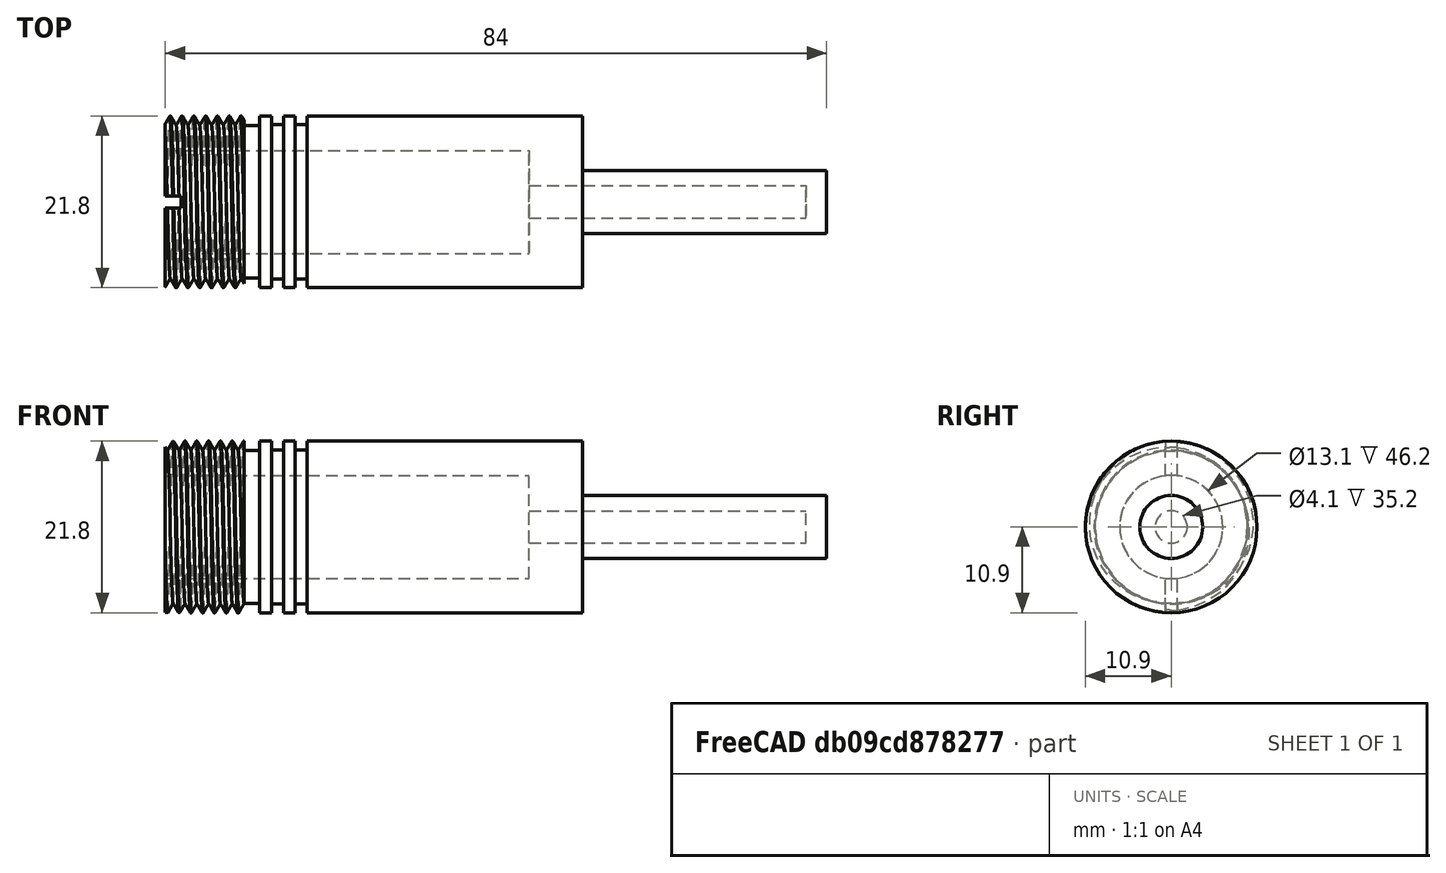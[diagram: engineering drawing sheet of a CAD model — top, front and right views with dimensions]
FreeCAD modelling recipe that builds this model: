
FCSTD DOCUMENT  (FreeCAD 0.17R13541 (Git))
Label: ERG-T-03-SH-01
License: All rights reserved
LicenseURL: http://en.wikipedia.org/wiki/All_rights_reserved
objects: Drawing::FeatureViewPython×25, Part::Cylinder×16, Part::Cut×11, Part::MultiFuse×4, Part::Helix×1, Sketcher::SketchObject×1, Part::Sweep×1, Part::Box×1, Drawing::FeatureViewPart×1, Drawing::FeaturePage×1
note: 35 computed .brp shape members not serialized (recipe doc carries the construction recipe); baked Part::Feature solids carry a one-line shape summary decoded from their .brp

FEATURE [Part::Cylinder] Cylinder072  label="Cylinder077"
  Angle = 360
  AttacherType = Attacher::AttachEngine3D
  Height = 18
  Placement = pos=(180.5,0,0) rot=(0,1,0;1.5708rad)
  Radius = 10.9
FEATURE [Part::Cylinder] Cylinder074  label="Cylinder083"
  Angle = 360
  AttacherType = Attacher::AttachEngine3D
  Height = 46.2
  Placement = pos=(180.5,0,0) rot=(0,1,0;1.5708rad)
  Radius = 6.55
FEATURE [Part::Cylinder] Cylinder075  label="Cylinder084"
  Angle = 360
  AttacherType = Attacher::AttachEngine3D
  Height = 53
  Placement = pos=(180.5,0,0) rot=(0,1,0;1.5708rad)
  Radius = 12.5
FEATURE [Part::Cylinder] Cylinder076  label="Cylinder085"
  Angle = 360
  AttacherType = Attacher::AttachEngine3D
  Height = 18
  Placement = pos=(180.5,0,0) rot=(0,1,0;1.5708rad)
  Radius = 12.5
FEATURE [Part::Cylinder] Cylinder077  label="Cylinder086"
  Angle = 360
  AttacherType = Attacher::AttachEngine3D
  Height = 31
  Placement = pos=(233.5,0,0) rot=(0,1,0;1.5708rad)
  Radius = 4
FEATURE [Part::Cut] Cut065
  Base = -> Cylinder076
  Tool = -> Cylinder072
FEATURE [Part::Cylinder] Cylinder080  label="Cylinder089"
  Angle = 360
  AttacherType = Attacher::AttachEngine3D
  Height = 35.2
  Placement = pos=(226.7,0,0) rot=(0,1,0;1.5708rad)
  Radius = 2.05
FEATURE [Part::MultiFuse] Fusion017  label="cavity"
  Shapes = -> [Cylinder080,Cylinder074]
FEATURE [Part::Helix] Helix019
  Angle = 0
  AttacherType = Attacher::AttachEngine3D
  Height = 17
  LocalCoord = 0
  Pitch = 1.5
  Placement = pos=(157,0,0) rot=(0,1,0;1.5708rad)
  Radius = 10.5
  Style = 1
FEATURE [Sketcher::SketchObject] Sketch023  label="T022"
  Placement = pos=(157,0,-11.01) rot=(1,0,0;1.5708rad)
  sketch-geometry (3):
    g0: LineSegment StartX=0 StartY=1.29904 StartZ=0 EndX=-0.75 EndY=0 EndZ=0
    g1: LineSegment StartX=0.75 StartY=0 StartZ=0 EndX=0 EndY=1.29904 EndZ=0
    g2: LineSegment StartX=-0.75 StartY=0 StartZ=0 EndX=0.75 EndY=0 EndZ=0
  constraints (9):
    c: PointOnObject(g1,g-1)
    c: Coincident(g1,g0)
    c: Coincident(g2,g0)
    c: Coincident(g2,g1)
    c: Horizontal(g2)
    c: Symmetric(g0,g1,g-2)
    c: Distance(g0,g1) = 1.5
    c: Angle(g1,g2) = 1.0472
    c: Angle(g2,g0) = 1.0472
FEATURE [Part::Sweep] Sweep016
  Frenet = true
  Sections = -> [Sketch023]
  Solid = true
  Spine = -> Helix019
  Transition = 1
FEATURE [Part::Cylinder] Cylinder084  label="Cylinder092"
  Angle = 360
  AttacherType = Attacher::AttachEngine3D
  Height = 1.5
  Placement = pos=(178,0,0) rot=(0,1,0;1.5708rad)
  Radius = 11
FEATURE [Part::Cylinder] Cylinder085  label="Cylinder093"
  Angle = 360
  AttacherType = Attacher::AttachEngine3D
  Height = 1.5
  Placement = pos=(178,0,0) rot=(0,1,0;1.5708rad)
  Radius = 9.8
FEATURE [Part::Cut] Cut071  label="circ2"
  Base = -> Cylinder084
  Placement = pos=(16,0,0) rot=(0,0,1;0rad)
  Tool = -> Cylinder085
FEATURE [Part::Cylinder] Cylinder086  label="Cylinder094"
  Angle = 360
  AttacherType = Attacher::AttachEngine3D
  Height = 2
  Placement = pos=(178,0,0) rot=(0,1,0;1.5708rad)
  Radius = 11
FEATURE [Part::Cylinder] Cylinder087  label="Cylinder095"
  Angle = 360
  AttacherType = Attacher::AttachEngine3D
  Height = 2
  Placement = pos=(178,0,0) rot=(0,1,0;1.5708rad)
  Radius = 9.7
FEATURE [Part::Cut] Cut072  label="circ1"
  Base = -> Cylinder086
  Placement = pos=(12.5,0,0) rot=(0,0,1;0rad)
  Tool = -> Cylinder087
FEATURE [Part::Cylinder] Cylinder088  label="Cylinder096"
  Angle = 360
  AttacherType = Attacher::AttachEngine3D
  Height = 10
  Placement = pos=(178,0,0) rot=(0,1,0;1.5708rad)
  Radius = 9
FEATURE [Part::Cylinder] Cylinder089  label="Cylinder097"
  Angle = 360
  AttacherType = Attacher::AttachEngine3D
  Height = 10
  Placement = pos=(178,0,0) rot=(0,1,0;1.5708rad)
  Radius = 11.5
FEATURE [Part::Cut] Cut074
  Base = -> Cylinder089
  Placement = pos=(-10.5,0,0) rot=(0,0,1;0rad)
  Tool = -> Cylinder088
FEATURE [Part::Box] Box  label="Cube"
  AttacherType = Attacher::AttachEngine3D
  Height = 30
  Length = 2
  Placement = pos=(180.5,-0.75,-15) rot=(0,0,1;0rad)
  Width = 1.5
FEATURE [Part::Cylinder] Cylinder091  label="Cylinder099"
  Angle = 360
  AttacherType = Attacher::AttachEngine3D
  Height = 35
  Placement = pos=(198.5,0,0) rot=(0,1,0;1.5708rad)
  Radius = 12.5
FEATURE [Part::Cylinder] Cylinder092  label="Cylinder100"
  Angle = 360
  AttacherType = Attacher::AttachEngine3D
  Height = 35
  Placement = pos=(198.5,0,0) rot=(0,1,0;1.5708rad)
  Radius = 10.9
FEATURE [Part::Cut] Cut
  Base = -> Cylinder091
  Tool = -> Cylinder092
FEATURE [Part::Cylinder] Cylinder093  label="Cylinder101"
  Angle = 360
  AttacherType = Attacher::AttachEngine3D
  Height = 1.5
  Placement = pos=(178,0,0) rot=(0,1,0;1.5708rad)
  Radius = 11
FEATURE [Part::Cylinder] Cylinder094  label="Cylinder102"
  Angle = 360
  AttacherType = Attacher::AttachEngine3D
  Height = 1.5
  Placement = pos=(178,0,0) rot=(0,1,0;1.5708rad)
  Radius = 9.8
FEATURE [Part::Cut] Cut076  label="circ3"
  Base = -> Cylinder093
  Placement = pos=(19,0,0) rot=(0,0,1;0rad)
  Tool = -> Cylinder094
FEATURE [Part::MultiFuse] Fusion019
  Shapes = -> [Cut,Cut065]
FEATURE [Part::MultiFuse] Fusion020
  Shapes = -> [Cylinder075,Cylinder077]
FEATURE [Part::Cut] Cut077  label="body"
  Base = -> Fusion020
  Tool = -> Fusion019
FEATURE [Part::Cut] Cut078  label="thread"
  Base = -> Sweep016
  Placement = pos=(23,0,0) rot=(0,0,1;0rad)
  Tool = -> Cut074
FEATURE [Part::MultiFuse] Fusion021  label="cutstuff"
  Shapes = -> [Cut078,Cut076,Cut072,Cut071]
FEATURE [Part::Cut] Cut079  label="outside"
  Base = -> Cut077
  Tool = -> Fusion021
FEATURE [Part::Cut] Cut080  label="holder01"
  Base = -> Cut079
  Tool = -> Fusion017
FEATURE [Part::Cut] Cut081  label="HOLDER"
  Base = -> Cut080
  Tool = -> Box
FEATURE [Drawing::FeatureViewPart] Ortho  label="Ortho_0_0"
  Direction = (0,1,0)
  HiddenWidth = 0.15
  LineWidth = 0.35
  Rotation = 90
  Scale = 2
  ShowHiddenLines = true
  ShowSmoothLines = false
  Source = -> Cut081
  Tolerance = 0.05
  ViewResult = <blob: 32842 chars omitted>
  Visible = false
  X = -316.2
  Y = 76.2849
FEATURE [Drawing::FeatureViewPython] dim001  # drawing view (typed FeaturePython)
  Rotation = 0
  ViewResult = <g> \n  <line x1="150.200000" y1="54.284900" x2="251.877041" y2="54.284900" style="stroke:rgb(255,0,0);stroke-width:0.10" />\n<line x1="150.200000" y1="98.284900" x2="251.877041" y2="98.284900" style="stroke:rgb(255,0,0);stroke-width:0.10" />\n<line x1="250.877041" y1="54.284900" x2="250.877041" y2="98.284900" style="stroke:rgb(255,0,0);stroke-width:0.10" /> \n  <polygon points="250.877041,98.284900 251.377041,96.284900 250.877041,95.784900 250.377041,96.284900" style="fill:rgb(255,0,0);stroke:rgb(255,0,0);stroke-width:0" /><polygon points="250.877041,54.284900 250.377041,56.284900 250.877041,56.784900 251.377041,56.284900" style="fill:rgb(255,0,0);stroke:rgb(255,0,0);stroke-width:0" /> \n  <text x="248.877041" y="76.284900" font-family="inherit" font-size="3.6" fill="rgb(0,0,0)" text-anchor="middle" transform="rotate(-90.000000 248.877041,76.284900)" >22</text> </g>
  Visible = false
  X = 0
  Y = 0
  arrowL1 = 2
  arrowL2 = 0.5
  arrowW = 1
  arrow_scheme = 0
  autoPlaceOffset = 2
  autoPlaceText = true
  click1_x = 250.877
  click1_y = 133.724
  click2_x = 250.877
  click2_y = 133.724
  comma_decimal_place = false
  dimension_line_overshoot = 1
  gap_datum_points = 0
  halfDimension_linear = false
  lineColor = rgb(255,0,0)
  strokeWidth = 0.1
  textFormat_linear = %(value)3.3f
  textRenderer_color = rgb(0,0,0)
  textRenderer_family = inherit
  textRenderer_size = 3.6
  unit_custom_scale = 1.2
  unit_scheme = 0
FEATURE [Drawing::FeatureViewPython] dim002  # drawing view (typed FeaturePython)
  Rotation = 0
  ViewResult = <g> \n  <line x1="138.200000" y1="101.284900" x2="263.684728" y2="101.284900" style="stroke:rgb(255,0,0);stroke-width:0.10" />\n<line x1="138.200000" y1="51.284900" x2="263.684728" y2="51.284900" style="stroke:rgb(255,0,0);stroke-width:0.10" />\n<line x1="262.684728" y1="101.284900" x2="262.684728" y2="51.284900" style="stroke:rgb(255,0,0);stroke-width:0.10" /> \n  <polygon points="262.684728,51.284900 262.184728,53.284900 262.684728,53.784900 263.184728,53.284900" style="fill:rgb(255,0,0);stroke:rgb(255,0,0);stroke-width:0" /><polygon points="262.684728,101.284900 263.184728,99.284900 262.684728,98.784900 262.184728,99.284900" style="fill:rgb(255,0,0);stroke:rgb(255,0,0);stroke-width:0" /> \n  <text x="260.684728" y="76.284900" font-family="inherit" font-size="3.6" fill="rgb(0,0,0)" text-anchor="middle" transform="rotate(-90.000000 260.684728,76.284900)" >25</text> </g>
  Visible = false
  X = 0
  Y = 0
  arrowL1 = 2
  arrowL2 = 0.5
  arrowW = 1
  arrow_scheme = 0
  autoPlaceOffset = 2
  autoPlaceText = true
  click1_x = 262.685
  click1_y = 70.4266
  click2_x = 262.685
  click2_y = 70.4266
  comma_decimal_place = false
  dimension_line_overshoot = 1
  gap_datum_points = 0
  halfDimension_linear = false
  lineColor = rgb(255,0,0)
  strokeWidth = 0.1
  textFormat_linear = %(value)3.3f
  textRenderer_color = rgb(0,0,0)
  textRenderer_family = inherit
  textRenderer_size = 3.6
  unit_custom_scale = 1.2
  unit_scheme = 0
FEATURE [Drawing::FeatureViewPython] dim003  # drawing view (typed FeaturePython)
  Rotation = 0
  ViewResult = <g> \n  <line x1="212.200000" y1="68.284900" x2="241.160157" y2="68.284900" style="stroke:rgb(255,0,0);stroke-width:0.10" />\n<line x1="212.200000" y1="84.284900" x2="241.160157" y2="84.284900" style="stroke:rgb(255,0,0);stroke-width:0.10" />\n<line x1="240.160157" y1="68.284900" x2="240.160157" y2="84.284900" style="stroke:rgb(255,0,0);stroke-width:0.10" /> \n  <polygon points="240.160157,84.284900 240.660157,82.284900 240.160157,81.784900 239.660157,82.284900" style="fill:rgb(255,0,0);stroke:rgb(255,0,0);stroke-width:0" /><polygon points="240.160157,68.284900 239.660157,70.284900 240.160157,70.784900 240.660157,70.284900" style="fill:rgb(255,0,0);stroke:rgb(255,0,0);stroke-width:0" /> \n  <text x="238.160157" y="76.284900" font-family="inherit" font-size="3.6" fill="rgb(0,0,0)" text-anchor="middle" transform="rotate(-90.000000 238.160157,76.284900)" >8</text> </g>
  Visible = false
  X = 0
  Y = 0
  arrowL1 = 2
  arrowL2 = 0.5
  arrowW = 1
  arrow_scheme = 0
  autoPlaceOffset = 2
  autoPlaceText = true
  click1_x = 240.16
  click1_y = 81.9652
  click2_x = 240.16
  click2_y = 81.9652
  comma_decimal_place = false
  dimension_line_overshoot = 1
  gap_datum_points = 0
  halfDimension_linear = false
  lineColor = rgb(255,0,0)
  strokeWidth = 0.1
  textFormat_linear = %(value)3.3f
  textRenderer_color = rgb(0,0,0)
  textRenderer_family = inherit
  textRenderer_size = 3.6
  unit_custom_scale = 1.2
  unit_scheme = 0
FEATURE [Drawing::FeatureViewPython] dim006  # drawing view (typed FeaturePython)
  Rotation = 0
  ViewResult = <g> \n  <line x1="207.600000" y1="72.184900" x2="232.266760" y2="72.184900" style="stroke:rgb(255,0,0);stroke-width:0.10" />\n<line x1="207.600000" y1="80.384900" x2="232.266760" y2="80.384900" style="stroke:rgb(255,0,0);stroke-width:0.10" />\n<line x1="231.266760" y1="72.184900" x2="231.266760" y2="80.384900" style="stroke:rgb(255,0,0);stroke-width:0.10" /> \n  <polygon points="231.266760,80.384900 231.766760,78.384900 231.266760,77.884900 230.766760,78.384900" style="fill:rgb(255,0,0);stroke:rgb(255,0,0);stroke-width:0" /><polygon points="231.266760,72.184900 230.766760,74.184900 231.266760,74.684900 231.766760,74.184900" style="fill:rgb(255,0,0);stroke:rgb(255,0,0);stroke-width:0" /> \n  <text x="229.266760" y="76.284900" font-family="inherit" font-size="3.6" fill="rgb(0,0,0)" text-anchor="middle" transform="rotate(-90.000000 229.266760,76.284900)" >4.1</text> </g>
  Visible = false
  X = 0
  Y = 0
  arrowL1 = 2
  arrowL2 = 0.5
  arrowW = 1
  arrow_scheme = 0
  autoPlaceOffset = 2
  autoPlaceText = true
  click1_x = 231.267
  click1_y = 77.6757
  click2_x = 231.267
  click2_y = 77.6757
  comma_decimal_place = false
  dimension_line_overshoot = 1
  gap_datum_points = 0
  halfDimension_linear = false
  lineColor = rgb(255,0,0)
  strokeWidth = 0.1
  textFormat_linear = %(value)3.3f
  textRenderer_color = rgb(0,0,0)
  textRenderer_family = inherit
  textRenderer_size = 3.6
  unit_custom_scale = 1.2
  unit_scheme = 0
FEATURE [Drawing::FeatureViewPython] dim004  # drawing view (typed FeaturePython)
  Rotation = 0
  ViewResult = <g> \n  <line x1="207.600000" y1="72.184900" x2="202.131464" y2="72.184900" style="stroke:rgb(255,0,0);stroke-width:0.10" />\n<line x1="207.600000" y1="80.384900" x2="202.131464" y2="80.384900" style="stroke:rgb(255,0,0);stroke-width:0.10" />\n<line x1="203.131464" y1="72.184900" x2="203.131464" y2="80.384900" style="stroke:rgb(255,0,0);stroke-width:0.10" /> \n  <polygon points="203.131464,80.384900 203.631464,78.384900 203.131464,77.884900 202.631464,78.384900" style="fill:rgb(255,0,0);stroke:rgb(255,0,0);stroke-width:0" /><polygon points="203.131464,72.184900 202.631464,74.184900 203.131464,74.684900 203.631464,74.184900" style="fill:rgb(255,0,0);stroke:rgb(255,0,0);stroke-width:0" /> \n  <text x="201.131464" y="76.284900" font-family="inherit" font-size="3.6" fill="rgb(0,0,0)" text-anchor="middle" transform="rotate(-90.000000 201.131464,76.284900)" >4.1</text> </g>
  Visible = false
  X = 0
  Y = 0
  arrowL1 = 2
  arrowL2 = 0.5
  arrowW = 1
  arrow_scheme = 0
  autoPlaceOffset = 2
  autoPlaceText = true
  click1_x = 203.131
  click1_y = 80.2658
  click2_x = 203.131
  click2_y = 80.2658
  comma_decimal_place = false
  dimension_line_overshoot = 1
  gap_datum_points = 0
  halfDimension_linear = false
  lineColor = rgb(255,0,0)
  strokeWidth = 0.1
  textFormat_linear = %(value)3.3f
  textRenderer_color = rgb(0,0,0)
  textRenderer_family = inherit
  textRenderer_size = 3.6
  unit_custom_scale = 1.2
  unit_scheme = 0
FEATURE [Drawing::FeatureViewPython] dim005  # drawing view (typed FeaturePython)
  Rotation = 0
  ViewResult = <g> \n  <line x1="137.200000" y1="63.184900" x2="127.267707" y2="63.184900" style="stroke:rgb(255,0,0);stroke-width:0.10" />\n<line x1="137.200000" y1="89.384900" x2="127.267707" y2="89.384900" style="stroke:rgb(255,0,0);stroke-width:0.10" />\n<line x1="128.267707" y1="63.184900" x2="128.267707" y2="89.384900" style="stroke:rgb(255,0,0);stroke-width:0.10" /> \n  <polygon points="128.267707,89.384900 128.767707,87.384900 128.267707,86.884900 127.767707,87.384900" style="fill:rgb(255,0,0);stroke:rgb(255,0,0);stroke-width:0" /><polygon points="128.267707,63.184900 127.767707,65.184900 128.267707,65.684900 128.767707,65.184900" style="fill:rgb(255,0,0);stroke:rgb(255,0,0);stroke-width:0" /> \n  <text x="126.267707" y="76.284900" font-family="inherit" font-size="3.6" fill="rgb(0,0,0)" text-anchor="middle" transform="rotate(-90.000000 126.267707,76.284900)" >13.1</text> </g>
  Visible = false
  X = 0
  Y = 0
  arrowL1 = 2
  arrowL2 = 0.5
  arrowW = 1
  arrow_scheme = 0
  autoPlaceOffset = 2
  autoPlaceText = true
  click1_x = 128.268
  click1_y = 88.9348
  click2_x = 128.268
  click2_y = 88.9348
  comma_decimal_place = false
  dimension_line_overshoot = 1
  gap_datum_points = 0
  halfDimension_linear = false
  lineColor = rgb(255,0,0)
  strokeWidth = 0.1
  textFormat_linear = %(value)3.3f
  textRenderer_color = rgb(0,0,0)
  textRenderer_family = inherit
  textRenderer_size = 3.6
  unit_custom_scale = 1.2
  unit_scheme = 0
FEATURE [Drawing::FeatureViewPython] dim007  # drawing view (typed FeaturePython)
  Rotation = 0
  ViewResult = <g> \n  <line x1="80.800000" y1="56.684900" x2="91.900891" y2="56.684900" style="stroke:rgb(255,0,0);stroke-width:0.10" />\n<line x1="80.800000" y1="95.926020" x2="91.900891" y2="95.926020" style="stroke:rgb(255,0,0);stroke-width:0.10" />\n<line x1="90.900891" y1="56.684900" x2="90.900891" y2="95.926020" style="stroke:rgb(255,0,0);stroke-width:0.10" /> \n  <polygon points="90.900891,95.926020 91.400891,93.926020 90.900891,93.426020 90.400891,93.926020" style="fill:rgb(255,0,0);stroke:rgb(255,0,0);stroke-width:0" /><polygon points="90.900891,56.684900 90.400891,58.684900 90.900891,59.184900 91.400891,58.684900" style="fill:rgb(255,0,0);stroke:rgb(255,0,0);stroke-width:0" /> \n  <text x="88.900891" y="76.305460" font-family="inherit" font-size="3.6" fill="rgb(0,0,0)" text-anchor="middle" transform="rotate(-90.000000 88.900891,76.305460)" >19.6</text> </g>
  Visible = false
  X = 0
  Y = 0
  arrowL1 = 2
  arrowL2 = 0.5
  arrowW = 1
  arrow_scheme = 0
  autoPlaceOffset = 2
  autoPlaceText = true
  click1_x = 90.9009
  click1_y = 93.3332
  click2_x = 90.9009
  click2_y = 93.3332
  comma_decimal_place = false
  dimension_line_overshoot = 1
  gap_datum_points = 0
  halfDimension_linear = false
  lineColor = rgb(255,0,0)
  strokeWidth = 0.1
  textFormat_linear = %(value)3.1f
  textRenderer_color = rgb(0,0,0)
  textRenderer_family = inherit
  textRenderer_size = 3.6
  unit_custom_scale = 1.2
  unit_scheme = 0
FEATURE [Drawing::FeatureViewPython] dim008  # drawing view (typed FeaturePython)
  Rotation = 0
  ViewResult = <g> \n  <line x1="77.800000" y1="54.484900" x2="98.633883" y2="54.484900" style="stroke:rgb(255,0,0);stroke-width:0.10" />\n<line x1="77.800000" y1="98.084900" x2="98.633883" y2="98.084900" style="stroke:rgb(255,0,0);stroke-width:0.10" />\n<line x1="97.633883" y1="54.484900" x2="97.633883" y2="98.084900" style="stroke:rgb(255,0,0);stroke-width:0.10" /> \n  <polygon points="97.633883,98.084900 98.133883,96.084900 97.633883,95.584900 97.133883,96.084900" style="fill:rgb(255,0,0);stroke:rgb(255,0,0);stroke-width:0" /><polygon points="97.633883,54.484900 97.133883,56.484900 97.633883,56.984900 98.133883,56.484900" style="fill:rgb(255,0,0);stroke:rgb(255,0,0);stroke-width:0" /> \n  <text x="95.633883" y="76.284900" font-family="inherit" font-size="3.6" fill="rgb(0,0,0)" text-anchor="middle" transform="rotate(-90.000000 95.633883,76.284900)" >21.8</text> </g>
  Visible = false
  X = 0
  Y = 0
  arrowL1 = 2
  arrowL2 = 0.5
  arrowW = 1
  arrow_scheme = 0
  autoPlaceOffset = 2
  autoPlaceText = true
  click1_x = 97.6339
  click1_y = 96.5836
  click2_x = 97.6339
  click2_y = 96.5836
  comma_decimal_place = false
  dimension_line_overshoot = 1
  gap_datum_points = 0
  halfDimension_linear = false
  lineColor = rgb(255,0,0)
  strokeWidth = 0.1
  textFormat_linear = %(value)3.3f
  textRenderer_color = rgb(0,0,0)
  textRenderer_family = inherit
  textRenderer_size = 3.6
  unit_custom_scale = 1.2
  unit_scheme = 0
FEATURE [Drawing::FeatureViewPython] dim009  # drawing view (typed FeaturePython)
  Rotation = 0
  ViewResult = <g> \n  <line x1="77.800000" y1="54.484900" x2="91.935645" y2="54.484900" style="stroke:rgb(255,0,0);stroke-width:0.10" />\n<line x1="77.800000" y1="56.684900" x2="91.935645" y2="56.684900" style="stroke:rgb(255,0,0);stroke-width:0.10" />\n<line x1="90.935645" y1="54.484900" x2="90.935645" y2="56.684900" style="stroke:rgb(255,0,0);stroke-width:0.10" /> \n  <polygon points="90.935645,56.684900 90.435645,58.684900 90.935645,59.184900 91.435645,58.684900" style="fill:rgb(255,0,0);stroke:rgb(255,0,0);stroke-width:0" /><polygon points="90.935645,54.484900 91.435645,52.484900 90.935645,51.984900 90.435645,52.484900" style="fill:rgb(255,0,0);stroke:rgb(255,0,0);stroke-width:0" /> \n  <text x="88.935645" y="55.584900" font-family="inherit" font-size="3.6" fill="rgb(0,0,0)" text-anchor="middle" transform="rotate(-90.000000 88.935645,55.584900)" >1.1</text> </g>
  Visible = false
  X = 0
  Y = 0
  arrowL1 = 2
  arrowL2 = 0.5
  arrowW = 1
  arrow_scheme = 0
  autoPlaceOffset = 2
  autoPlaceText = true
  click1_x = 90.9356
  click1_y = 59.3866
  click2_x = 90.9356
  click2_y = 59.3866
  comma_decimal_place = false
  dimension_line_overshoot = 1
  gap_datum_points = 0
  halfDimension_linear = false
  lineColor = rgb(255,0,0)
  strokeWidth = 0.1
  textFormat_linear = %(value)3.3f
  textRenderer_color = rgb(0,0,0)
  textRenderer_family = inherit
  textRenderer_size = 3.6
  unit_custom_scale = 1.2
  unit_scheme = 0
FEATURE [Drawing::FeatureViewPython] dim010  # drawing view (typed FeaturePython)
  Rotation = 0
  ViewResult = <g> \n  <line x1="150.200000" y1="68.284900" x2="150.200000" y2="38.450690" style="stroke:rgb(255,0,0);stroke-width:0.10" />\n<line x1="212.200000" y1="68.284900" x2="212.200000" y2="38.450690" style="stroke:rgb(255,0,0);stroke-width:0.10" />\n<line x1="150.200000" y1="39.450690" x2="212.200000" y2="39.450690" style="stroke:rgb(255,0,0);stroke-width:0.10" /> \n  <polygon points="212.200000,39.450690 210.200000,38.950690 209.700000,39.450690 210.200000,39.950690" style="fill:rgb(255,0,0);stroke:rgb(255,0,0);stroke-width:0" /><polygon points="150.200000,39.450690 152.200000,39.950690 152.700000,39.450690 152.200000,38.950690" style="fill:rgb(255,0,0);stroke:rgb(255,0,0);stroke-width:0" /> \n  <text x="181.200000" y="37.450690" font-family="inherit" font-size="3.6" fill="rgb(0,0,0)" text-anchor="middle" transform="rotate(0.000000 181.200000,37.450690)" >31</text> </g>
  Visible = false
  X = 0
  Y = 0
  arrowL1 = 2
  arrowL2 = 0.5
  arrowW = 1
  arrow_scheme = 0
  autoPlaceOffset = 2
  autoPlaceText = true
  click1_x = 188.487
  click1_y = 39.4507
  click2_x = 188.487
  click2_y = 39.4507
  comma_decimal_place = false
  dimension_line_overshoot = 1
  gap_datum_points = 0
  halfDimension_linear = false
  lineColor = rgb(255,0,0)
  strokeWidth = 0.1
  textFormat_linear = %(value)3.3f
  textRenderer_color = rgb(0,0,0)
  textRenderer_family = inherit
  textRenderer_size = 3.6
  unit_custom_scale = 1.2
  unit_scheme = 0
FEATURE [Drawing::FeatureViewPython] dim011  # drawing view (typed FeaturePython)
  Rotation = 0
  ViewResult = <g> \n  <line x1="138.200000" y1="54.284900" x2="138.200000" y2="38.450690" style="stroke:rgb(255,0,0);stroke-width:0.10" />\n<line x1="150.200000" y1="54.284900" x2="150.200000" y2="38.450690" style="stroke:rgb(255,0,0);stroke-width:0.10" />\n<line x1="138.200000" y1="39.450690" x2="150.200000" y2="39.450690" style="stroke:rgb(255,0,0);stroke-width:0.10" /> \n  <polygon points="150.200000,39.450690 148.200000,38.950690 147.700000,39.450690 148.200000,39.950690" style="fill:rgb(255,0,0);stroke:rgb(255,0,0);stroke-width:0" /><polygon points="138.200000,39.450690 140.200000,39.950690 140.700000,39.450690 140.200000,38.950690" style="fill:rgb(255,0,0);stroke:rgb(255,0,0);stroke-width:0" /> \n  <text x="144.200000" y="37.450690" font-family="inherit" font-size="3.6" fill="rgb(0,0,0)" text-anchor="middle" transform="rotate(0.000000 144.200000,37.450690)" >6</text> </g>
  Visible = false
  X = 0
  Y = 0
  arrowL1 = 2
  arrowL2 = 0.5
  arrowW = 1
  arrow_scheme = 0
  autoPlaceOffset = 2
  autoPlaceText = true
  click1_x = 144.088
  click1_y = 39.4507
  click2_x = 144.088
  click2_y = 39.4507
  comma_decimal_place = false
  dimension_line_overshoot = 1
  gap_datum_points = 0
  halfDimension_linear = false
  lineColor = rgb(255,0,0)
  strokeWidth = 0.1
  textFormat_linear = %(value)3.3f
  textRenderer_color = rgb(0,0,0)
  textRenderer_family = inherit
  textRenderer_size = 3.6
  unit_custom_scale = 1.2
  unit_scheme = 0
FEATURE [Drawing::FeatureViewPython] dim012  # drawing view (typed FeaturePython)
  Rotation = 0
  ViewResult = <g> \n  <line x1="80.800000" y1="51.284900" x2="80.800000" y2="38.450690" style="stroke:rgb(255,0,0);stroke-width:0.10" />\n<line x1="138.200000" y1="51.284900" x2="138.200000" y2="38.450690" style="stroke:rgb(255,0,0);stroke-width:0.10" />\n<line x1="80.800000" y1="39.450690" x2="138.200000" y2="39.450690" style="stroke:rgb(255,0,0);stroke-width:0.10" /> \n  <polygon points="138.200000,39.450690 136.200000,38.950690 135.700000,39.450690 136.200000,39.950690" style="fill:rgb(255,0,0);stroke:rgb(255,0,0);stroke-width:0" /><polygon points="80.800000,39.450690 82.800000,39.950690 83.300000,39.450690 82.800000,38.950690" style="fill:rgb(255,0,0);stroke:rgb(255,0,0);stroke-width:0" /> \n  <text x="109.500000" y="37.450690" font-family="inherit" font-size="3.6" fill="rgb(0,0,0)" text-anchor="middle" transform="rotate(0.000000 109.500000,37.450690)" >28.7</text> </g>
  Visible = false
  X = 0
  Y = 0
  arrowL1 = 2
  arrowL2 = 0.5
  arrowW = 1
  arrow_scheme = 0
  autoPlaceOffset = 2
  autoPlaceText = true
  click1_x = 122.825
  click1_y = 39.4507
  click2_x = 122.825
  click2_y = 39.4507
  comma_decimal_place = false
  dimension_line_overshoot = 1
  gap_datum_points = 0
  halfDimension_linear = false
  lineColor = rgb(255,0,0)
  strokeWidth = 0.1
  textFormat_linear = %(value)3.3f
  textRenderer_color = rgb(0,0,0)
  textRenderer_family = inherit
  textRenderer_size = 3.6
  unit_custom_scale = 1.2
  unit_scheme = 0
FEATURE [Drawing::FeatureViewPython] dim013  # drawing view (typed FeaturePython)
  Rotation = 0
  ViewResult = <g> \n  <line x1="64.800000" y1="56.845400" x2="64.800000" y2="38.469263" style="stroke:rgb(255,0,0);stroke-width:0.10" />\n<line x1="80.800000" y1="51.284900" x2="80.800000" y2="38.469263" style="stroke:rgb(255,0,0);stroke-width:0.10" />\n<line x1="64.800000" y1="39.469263" x2="80.800000" y2="39.469263" style="stroke:rgb(255,0,0);stroke-width:0.10" /> \n  <polygon points="80.800000,39.469263 78.800000,38.969263 78.300000,39.469263 78.800000,39.969263" style="fill:rgb(255,0,0);stroke:rgb(255,0,0);stroke-width:0" /><polygon points="64.800000,39.469263 66.800000,39.969263 67.300000,39.469263 66.800000,38.969263" style="fill:rgb(255,0,0);stroke:rgb(255,0,0);stroke-width:0" /> \n  <text x="72.800000" y="37.469263" font-family="inherit" font-size="3.6" fill="rgb(0,0,0)" text-anchor="middle" transform="rotate(0.000000 72.800000,37.469263)" >8</text> </g>
  Visible = false
  X = 0
  Y = 0
  arrowL1 = 2
  arrowL2 = 0.5
  arrowW = 1
  arrow_scheme = 0
  autoPlaceOffset = 2
  autoPlaceText = true
  click1_x = 80.0662
  click1_y = 39.4693
  click2_x = 80.0662
  click2_y = 39.4693
  comma_decimal_place = false
  dimension_line_overshoot = 1
  gap_datum_points = 0
  halfDimension_linear = false
  lineColor = rgb(255,0,0)
  strokeWidth = 0.1
  textFormat_linear = %(value)3.3f
  textRenderer_color = rgb(0,0,0)
  textRenderer_family = inherit
  textRenderer_size = 3.6
  unit_custom_scale = 1.2
  unit_scheme = 0
FEATURE [Drawing::FeatureViewPython] dim014  # drawing view (typed FeaturePython)
  Rotation = 0
  ViewResult = <g> \n  <line x1="64.800000" y1="56.845400" x2="64.800000" y2="38.492082" style="stroke:rgb(255,0,0);stroke-width:0.10" />\n<line x1="44.800000" y1="54.536500" x2="44.800000" y2="38.492082" style="stroke:rgb(255,0,0);stroke-width:0.10" />\n<line x1="64.800000" y1="39.492082" x2="44.800000" y2="39.492082" style="stroke:rgb(255,0,0);stroke-width:0.10" /> \n  <polygon points="44.800000,39.492082 46.800000,39.992082 47.300000,39.492082 46.800000,38.992082" style="fill:rgb(255,0,0);stroke:rgb(255,0,0);stroke-width:0" /><polygon points="64.800000,39.492082 62.800000,38.992082 62.300000,39.492082 62.800000,39.992082" style="fill:rgb(255,0,0);stroke:rgb(255,0,0);stroke-width:0" /> \n  <text x="54.800000" y="37.492082" font-family="inherit" font-size="3.6" fill="rgb(0,0,0)" text-anchor="middle" transform="rotate(0.000000 54.800000,37.492082)" >10</text> </g>
  Visible = false
  X = 0
  Y = 0
  arrowL1 = 2
  arrowL2 = 0.5
  arrowW = 1
  arrow_scheme = 0
  autoPlaceOffset = 2
  autoPlaceText = true
  click1_x = 46.7621
  click1_y = 39.4921
  click2_x = 46.7621
  click2_y = 39.4921
  comma_decimal_place = false
  dimension_line_overshoot = 1
  gap_datum_points = 0
  halfDimension_linear = false
  lineColor = rgb(255,0,0)
  strokeWidth = 0.1
  textFormat_linear = %(value)3.3f
  textRenderer_color = rgb(0,0,0)
  textRenderer_family = inherit
  textRenderer_size = 3.6
  unit_custom_scale = 1.2
  unit_scheme = 0
FEATURE [Drawing::FeatureViewPython] dim015  # drawing view (typed FeaturePython)
  Rotation = 0
  ViewResult = <g> \n  <line x1="44.800000" y1="54.536500" x2="44.800000" y2="26.268317" style="stroke:rgb(255,0,0);stroke-width:0.10" />\n<line x1="212.200000" y1="68.284900" x2="212.200000" y2="26.268317" style="stroke:rgb(255,0,0);stroke-width:0.10" />\n<line x1="44.800000" y1="27.268317" x2="212.200000" y2="27.268317" style="stroke:rgb(255,0,0);stroke-width:0.10" /> \n  <polygon points="212.200000,27.268317 210.200000,26.768317 209.700000,27.268317 210.200000,27.768317" style="fill:rgb(255,0,0);stroke:rgb(255,0,0);stroke-width:0" /><polygon points="44.800000,27.268317 46.800000,27.768317 47.300000,27.268317 46.800000,26.768317" style="fill:rgb(255,0,0);stroke:rgb(255,0,0);stroke-width:0" /> \n  <text x="128.500000" y="25.268317" font-family="inherit" font-size="3.6" fill="rgb(0,0,0)" text-anchor="middle" transform="rotate(0.000000 128.500000,25.268317)" >83.7</text> </g>
  Visible = false
  X = 0
  Y = 0
  arrowL1 = 2
  arrowL2 = 0.5
  arrowW = 1
  arrow_scheme = 0
  autoPlaceOffset = 2
  autoPlaceText = true
  click1_x = 209.701
  click1_y = 27.2683
  click2_x = 209.701
  click2_y = 27.2683
  comma_decimal_place = false
  dimension_line_overshoot = 1
  gap_datum_points = 0
  halfDimension_linear = false
  lineColor = rgb(255,0,0)
  strokeWidth = 0.1
  textFormat_linear = %(value)3.3f
  textRenderer_color = rgb(0,0,0)
  textRenderer_family = inherit
  textRenderer_size = 3.6
  unit_custom_scale = 1.2
  unit_scheme = 0
FEATURE [Drawing::FeatureViewPython] dim016  # drawing view (typed FeaturePython)
  Rotation = 0
  ViewResult = <g> \n  <line x1="137.200000" y1="89.384900" x2="137.200000" y2="115.632444" style="stroke:rgb(255,0,0);stroke-width:0.10" />\n<line x1="207.600000" y1="80.384900" x2="207.600000" y2="115.632444" style="stroke:rgb(255,0,0);stroke-width:0.10" />\n<line x1="137.200000" y1="114.632444" x2="207.600000" y2="114.632444" style="stroke:rgb(255,0,0);stroke-width:0.10" /> \n  <polygon points="207.600000,114.632444 205.600000,114.132444 205.100000,114.632444 205.600000,115.132444" style="fill:rgb(255,0,0);stroke:rgb(255,0,0);stroke-width:0" /><polygon points="137.200000,114.632444 139.200000,115.132444 139.700000,114.632444 139.200000,114.132444" style="fill:rgb(255,0,0);stroke:rgb(255,0,0);stroke-width:0" /> \n  <text x="172.400000" y="112.632444" font-family="inherit" font-size="3.6" fill="rgb(0,0,0)" text-anchor="middle" transform="rotate(0.000000 172.400000,112.632444)" >35.2</text> </g>
  Visible = false
  X = 0
  Y = 0
  arrowL1 = 2
  arrowL2 = 0.5
  arrowW = 1
  arrow_scheme = 0
  autoPlaceOffset = 2
  autoPlaceText = true
  click1_x = 146.76
  click1_y = 114.632
  click2_x = 146.76
  click2_y = 114.632
  comma_decimal_place = false
  dimension_line_overshoot = 1
  gap_datum_points = 0
  halfDimension_linear = false
  lineColor = rgb(255,0,0)
  strokeWidth = 0.1
  textFormat_linear = %(value)3.3f
  textRenderer_color = rgb(0,0,0)
  textRenderer_family = inherit
  textRenderer_size = 3.6
  unit_custom_scale = 1.2
  unit_scheme = 0
FEATURE [Drawing::FeatureViewPython] dim017  # drawing view (typed FeaturePython)
  Rotation = 0
  ViewResult = <g> \n  <line x1="137.200000" y1="89.384900" x2="137.200000" y2="115.741328" style="stroke:rgb(255,0,0);stroke-width:0.10" />\n<line x1="44.800000" y1="89.298740" x2="44.800000" y2="115.741328" style="stroke:rgb(255,0,0);stroke-width:0.10" />\n<line x1="137.200000" y1="114.741328" x2="44.800000" y2="114.741328" style="stroke:rgb(255,0,0);stroke-width:0.10" /> \n  <polygon points="44.800000,114.741328 46.800000,115.241328 47.300000,114.741328 46.800000,114.241328" style="fill:rgb(255,0,0);stroke:rgb(255,0,0);stroke-width:0" /><polygon points="137.200000,114.741328 135.200000,114.241328 134.700000,114.741328 135.200000,115.241328" style="fill:rgb(255,0,0);stroke:rgb(255,0,0);stroke-width:0" /> \n  <text x="91.000000" y="112.741328" font-family="inherit" font-size="3.6" fill="rgb(0,0,0)" text-anchor="middle" transform="rotate(0.000000 91.000000,112.741328)" >46.2</text> </g>
  Visible = false
  X = 0
  Y = 0
  arrowL1 = 2
  arrowL2 = 0.5
  arrowW = 1
  arrow_scheme = 0
  autoPlaceOffset = 2
  autoPlaceText = true
  click1_x = 58.1525
  click1_y = 114.741
  click2_x = 58.1525
  click2_y = 114.741
  comma_decimal_place = false
  dimension_line_overshoot = 1
  gap_datum_points = 0
  halfDimension_linear = false
  lineColor = rgb(255,0,0)
  strokeWidth = 0.1
  textFormat_linear = %(value)3.3f
  textRenderer_color = rgb(0,0,0)
  textRenderer_family = inherit
  textRenderer_size = 3.6
  unit_custom_scale = 1.2
  unit_scheme = 0
FEATURE [Drawing::FeatureViewPython] dim018  # drawing view (typed FeaturePython)
  Rotation = 0
  ViewResult = <g> \n  <line x1="77.800000" y1="95.884900" x2="77.800000" y2="107.860093" style="stroke:rgb(255,0,0);stroke-width:0.10" />\n<line x1="80.800000" y1="95.884900" x2="80.800000" y2="107.860093" style="stroke:rgb(255,0,0);stroke-width:0.10" />\n<line x1="77.800000" y1="106.860093" x2="80.800000" y2="106.860093" style="stroke:rgb(255,0,0);stroke-width:0.10" /> \n  <polygon points="80.800000,106.860093 82.800000,107.360093 83.300000,106.860093 82.800000,106.360093" style="fill:rgb(255,0,0);stroke:rgb(255,0,0);stroke-width:0" /><polygon points="77.800000,106.860093 75.800000,106.360093 75.300000,106.860093 75.800000,107.360093" style="fill:rgb(255,0,0);stroke:rgb(255,0,0);stroke-width:0" /> \n  <text x="79.300000" y="104.860093" font-family="inherit" font-size="3.6" fill="rgb(0,0,0)" text-anchor="middle" transform="rotate(0.000000 79.300000,104.860093)" >1.5</text> </g>
  Visible = false
  X = 0
  Y = 0
  arrowL1 = 2
  arrowL2 = 0.5
  arrowW = 1
  arrow_scheme = 0
  autoPlaceOffset = 2
  autoPlaceText = true
  click1_x = 78.3955
  click1_y = 106.86
  click2_x = 78.3955
  click2_y = 106.86
  comma_decimal_place = false
  dimension_line_overshoot = 1
  gap_datum_points = 0
  halfDimension_linear = false
  lineColor = rgb(255,0,0)
  strokeWidth = 0.1
  textFormat_linear = %(value)3.3f
  textRenderer_color = rgb(0,0,0)
  textRenderer_family = inherit
  textRenderer_size = 3.6
  unit_custom_scale = 1.2
  unit_scheme = 0
FEATURE [Drawing::FeatureViewPython] dim019  # drawing view (typed FeaturePython)
  Rotation = 0
  ViewResult = <g> \n  <line x1="64.800000" y1="95.684900" x2="64.800000" y2="107.860093" style="stroke:rgb(255,0,0);stroke-width:0.10" />\n<line x1="68.800000" y1="95.684900" x2="68.800000" y2="107.860093" style="stroke:rgb(255,0,0);stroke-width:0.10" />\n<line x1="64.800000" y1="106.860093" x2="68.800000" y2="106.860093" style="stroke:rgb(255,0,0);stroke-width:0.10" /> \n  <polygon points="68.800000,106.860093 70.800000,107.360093 71.300000,106.860093 70.800000,106.360093" style="fill:rgb(255,0,0);stroke:rgb(255,0,0);stroke-width:0" /><polygon points="64.800000,106.860093 62.800000,106.360093 62.300000,106.860093 62.800000,107.360093" style="fill:rgb(255,0,0);stroke:rgb(255,0,0);stroke-width:0" /> \n  <text x="66.800000" y="104.860093" font-family="inherit" font-size="3.6" fill="rgb(0,0,0)" text-anchor="middle" transform="rotate(0.000000 66.800000,104.860093)" >2</text> </g>
  Visible = false
  X = 0
  Y = 0
  arrowL1 = 2
  arrowL2 = 0.5
  arrowW = 1
  arrow_scheme = 0
  autoPlaceOffset = 2
  autoPlaceText = true
  click1_x = 66.3928
  click1_y = 106.86
  click2_x = 66.3928
  click2_y = 106.86
  comma_decimal_place = false
  dimension_line_overshoot = 1
  gap_datum_points = 0
  halfDimension_linear = false
  lineColor = rgb(255,0,0)
  strokeWidth = 0.1
  textFormat_linear = %(value)3.3f
  textRenderer_color = rgb(0,0,0)
  textRenderer_family = inherit
  textRenderer_size = 3.6
  unit_custom_scale = 1.2
  unit_scheme = 0
FEATURE [Drawing::FeatureViewPython] dim020  # drawing view (typed FeaturePython)
  Rotation = 0
  ViewResult = <g> \n  <line x1="71.800000" y1="95.884900" x2="71.800000" y2="113.906242" style="stroke:rgb(255,0,0);stroke-width:0.10" />\n<line x1="74.800000" y1="95.884900" x2="74.800000" y2="113.906242" style="stroke:rgb(255,0,0);stroke-width:0.10" />\n<line x1="71.800000" y1="112.906242" x2="74.800000" y2="112.906242" style="stroke:rgb(255,0,0);stroke-width:0.10" /> \n  <polygon points="74.800000,112.906242 76.800000,113.406242 77.300000,112.906242 76.800000,112.406242" style="fill:rgb(255,0,0);stroke:rgb(255,0,0);stroke-width:0" /><polygon points="71.800000,112.906242 69.800000,112.406242 69.300000,112.906242 69.800000,113.406242" style="fill:rgb(255,0,0);stroke:rgb(255,0,0);stroke-width:0" /> \n  <text x="73.300000" y="110.906242" font-family="inherit" font-size="3.6" fill="rgb(0,0,0)" text-anchor="middle" transform="rotate(0.000000 73.300000,110.906242)" >1.5</text> </g>
  Visible = false
  X = 0
  Y = 0
  arrowL1 = 2
  arrowL2 = 0.5
  arrowW = 1
  arrow_scheme = 0
  autoPlaceOffset = 2
  autoPlaceText = true
  click1_x = 71.8119
  click1_y = 112.906
  click2_x = 71.8119
  click2_y = 112.906
  comma_decimal_place = false
  dimension_line_overshoot = 1
  gap_datum_points = 0
  halfDimension_linear = false
  lineColor = rgb(255,0,0)
  strokeWidth = 0.1
  textFormat_linear = %(value)3.3f
  textRenderer_color = rgb(0,0,0)
  textRenderer_family = inherit
  textRenderer_size = 3.6
  unit_custom_scale = 1.2
  unit_scheme = 0
FEATURE [Drawing::FeatureViewPython] dim021  # drawing view (typed FeaturePython)
  Rotation = 0
  ViewResult = <g> \n  <line x1="68.800000" y1="54.484900" x2="68.800000" y2="46.989756" style="stroke:rgb(255,0,0);stroke-width:0.10" />\n<line x1="71.800000" y1="54.484900" x2="71.800000" y2="46.989756" style="stroke:rgb(255,0,0);stroke-width:0.10" />\n<line x1="68.800000" y1="47.989756" x2="71.800000" y2="47.989756" style="stroke:rgb(255,0,0);stroke-width:0.10" /> \n  <polygon points="71.800000,47.989756 73.800000,48.489756 74.300000,47.989756 73.800000,47.489756" style="fill:rgb(255,0,0);stroke:rgb(255,0,0);stroke-width:0" /><polygon points="68.800000,47.989756 66.800000,47.489756 66.300000,47.989756 66.800000,48.489756" style="fill:rgb(255,0,0);stroke:rgb(255,0,0);stroke-width:0" /> \n  <text x="70.300000" y="45.989756" font-family="inherit" font-size="3.6" fill="rgb(0,0,0)" text-anchor="middle" transform="rotate(0.000000 70.300000,45.989756)" >1.5</text> </g>
  Visible = false
  X = 0
  Y = 0
  arrowL1 = 2
  arrowL2 = 0.5
  arrowW = 1
  arrow_scheme = 0
  autoPlaceOffset = 2
  autoPlaceText = true
  click1_x = 70.7233
  click1_y = 47.9898
  click2_x = 70.7233
  click2_y = 47.9898
  comma_decimal_place = false
  dimension_line_overshoot = 1
  gap_datum_points = 0
  halfDimension_linear = false
  lineColor = rgb(255,0,0)
  strokeWidth = 0.1
  textFormat_linear = %(value)3.3f
  textRenderer_color = rgb(0,0,0)
  textRenderer_family = inherit
  textRenderer_size = 3.6
  unit_custom_scale = 1.2
  unit_scheme = 0
FEATURE [Drawing::FeatureViewPython] dim022  # drawing view (typed FeaturePython)
  Rotation = 0
  ViewResult = <g> \n  <line x1="74.800000" y1="54.484900" x2="74.800000" y2="47.051959" style="stroke:rgb(255,0,0);stroke-width:0.10" />\n<line x1="77.800000" y1="54.484900" x2="77.800000" y2="47.051959" style="stroke:rgb(255,0,0);stroke-width:0.10" />\n<line x1="74.800000" y1="48.051959" x2="77.800000" y2="48.051959" style="stroke:rgb(255,0,0);stroke-width:0.10" /> \n  <polygon points="77.800000,48.051959 79.800000,48.551959 80.300000,48.051959 79.800000,47.551959" style="fill:rgb(255,0,0);stroke:rgb(255,0,0);stroke-width:0" /><polygon points="74.800000,48.051959 72.800000,47.551959 72.300000,48.051959 72.800000,48.551959" style="fill:rgb(255,0,0);stroke:rgb(255,0,0);stroke-width:0" /> \n  <text x="76.300000" y="46.051959" font-family="inherit" font-size="3.6" fill="rgb(0,0,0)" text-anchor="middle" transform="rotate(0.000000 76.300000,46.051959)" >1.5</text> </g>
  Visible = false
  X = 0
  Y = 0
  arrowL1 = 2
  arrowL2 = 0.5
  arrowW = 1
  arrow_scheme = 0
  autoPlaceOffset = 2
  autoPlaceText = true
  click1_x = 76.8815
  click1_y = 48.052
  click2_x = 76.8815
  click2_y = 48.052
  comma_decimal_place = false
  dimension_line_overshoot = 1
  gap_datum_points = 0
  halfDimension_linear = false
  lineColor = rgb(255,0,0)
  strokeWidth = 0.1
  textFormat_linear = %(value)3.3f
  textRenderer_color = rgb(0,0,0)
  textRenderer_family = inherit
  textRenderer_size = 3.6
  unit_custom_scale = 1.2
  unit_scheme = 0
FEATURE [Drawing::FeatureViewPython] dim023  # drawing view (typed FeaturePython)
  Rotation = 0
  ViewResult = <g> \n  <line x1="48.800000" y1="96.589700" x2="48.800000" y2="108.031355" style="stroke:rgb(255,0,0);stroke-width:0.10" />\n<line x1="44.800000" y1="96.455700" x2="44.800000" y2="108.031355" style="stroke:rgb(255,0,0);stroke-width:0.10" />\n<line x1="48.800000" y1="107.031355" x2="44.800000" y2="107.031355" style="stroke:rgb(255,0,0);stroke-width:0.10" /> \n  <polygon points="44.800000,107.031355 42.800000,106.531355 42.300000,107.031355 42.800000,107.531355" style="fill:rgb(255,0,0);stroke:rgb(255,0,0);stroke-width:0" /><polygon points="48.800000,107.031355 50.800000,107.531355 51.300000,107.031355 50.800000,106.531355" style="fill:rgb(255,0,0);stroke:rgb(255,0,0);stroke-width:0" /> \n  <text x="46.800000" y="105.031355" font-family="inherit" font-size="3.6" fill="rgb(0,0,0)" text-anchor="middle" transform="rotate(0.000000 46.800000,105.031355)" >2</text> </g>
  Visible = false
  X = 0
  Y = 0
  arrowL1 = 2
  arrowL2 = 0.5
  arrowW = 1
  arrow_scheme = 0
  autoPlaceOffset = 2
  autoPlaceText = true
  click1_x = 47.2525
  click1_y = 107.031
  click2_x = 47.2525
  click2_y = 107.031
  comma_decimal_place = false
  dimension_line_overshoot = 1
  gap_datum_points = 0
  halfDimension_linear = false
  lineColor = rgb(255,0,0)
  strokeWidth = 0.1
  textFormat_linear = %(value)3.3f
  textRenderer_color = rgb(0,0,0)
  textRenderer_family = inherit
  textRenderer_size = 3.6
  unit_custom_scale = 1.2
  unit_scheme = 0
FEATURE [Drawing::FeatureViewPython] dim025  # drawing view (typed FeaturePython)
  Rotation = 0
  ViewResult = <g> \n  <line x1="207.600000" y1="72.184900" x2="222.148073" y2="72.184900" style="stroke:rgb(255,0,0);stroke-width:0.10" />\n<line x1="212.200000" y1="68.284900" x2="222.148073" y2="68.284900" style="stroke:rgb(255,0,0);stroke-width:0.10" />\n<line x1="221.148073" y1="72.184900" x2="221.148073" y2="68.284900" style="stroke:rgb(255,0,0);stroke-width:0.10" /> \n  <polygon points="221.148073,68.284900 221.648073,66.284900 221.148073,65.784900 220.648073,66.284900" style="fill:rgb(255,0,0);stroke:rgb(255,0,0);stroke-width:0" /><polygon points="221.148073,72.184900 220.648073,74.184900 221.148073,74.684900 221.648073,74.184900" style="fill:rgb(255,0,0);stroke:rgb(255,0,0);stroke-width:0" /> \n  <text x="219.148073" y="70.234900" font-family="inherit" font-size="3.6" fill="rgb(0,0,0)" text-anchor="middle" transform="rotate(-90.000000 219.148073,70.234900)" >1.95</text> </g>
  Visible = false
  X = 0
  Y = 0
  arrowL1 = 2
  arrowL2 = 0.5
  arrowW = 1
  arrow_scheme = 0
  autoPlaceOffset = 2
  autoPlaceText = true
  click1_x = 221.148
  click1_y = 71.0361
  click2_x = 221.148
  click2_y = 71.0361
  comma_decimal_place = false
  dimension_line_overshoot = 1
  gap_datum_points = 0
  halfDimension_linear = false
  lineColor = rgb(255,0,0)
  strokeWidth = 0.1
  textFormat_linear = %(value)3.3f
  textRenderer_color = rgb(0,0,0)
  textRenderer_family = inherit
  textRenderer_size = 3.6
  unit_custom_scale = 1.2
  unit_scheme = 0
FEATURE [Drawing::FeatureViewPython] dim026  # drawing view (typed FeaturePython)
  Rotation = 0
  ViewResult = <g> \n  <line x1="207.600000" y1="72.184900" x2="207.600000" y2="61.407871" style="stroke:rgb(255,0,0);stroke-width:0.10" />\n<line x1="212.200000" y1="68.284900" x2="212.200000" y2="61.407871" style="stroke:rgb(255,0,0);stroke-width:0.10" />\n<line x1="207.600000" y1="62.407871" x2="212.200000" y2="62.407871" style="stroke:rgb(255,0,0);stroke-width:0.10" /> \n  <polygon points="212.200000,62.407871 214.200000,62.907871 214.700000,62.407871 214.200000,61.907871" style="fill:rgb(255,0,0);stroke:rgb(255,0,0);stroke-width:0" /><polygon points="207.600000,62.407871 205.600000,61.907871 205.100000,62.407871 205.600000,62.907871" style="fill:rgb(255,0,0);stroke:rgb(255,0,0);stroke-width:0" /> \n  <text x="209.900000" y="60.407871" font-family="inherit" font-size="3.6" fill="rgb(0,0,0)" text-anchor="middle" transform="rotate(0.000000 209.900000,60.407871)" >2.3</text> </g>
  Visible = false
  X = 0
  Y = 0
  arrowL1 = 2
  arrowL2 = 0.5
  arrowW = 1
  arrow_scheme = 0
  autoPlaceOffset = 2
  autoPlaceText = true
  click1_x = 211.894
  click1_y = 62.4079
  click2_x = 211.894
  click2_y = 62.4079
  comma_decimal_place = false
  dimension_line_overshoot = 1
  gap_datum_points = 0
  halfDimension_linear = false
  lineColor = rgb(255,0,0)
  strokeWidth = 0.1
  textFormat_linear = %(value)3.3f
  textRenderer_color = rgb(0,0,0)
  textRenderer_family = inherit
  textRenderer_size = 3.6
  unit_custom_scale = 1.2
  unit_scheme = 0
FEATURE [Drawing::FeaturePage] Page  label="PROJECTION"
  EditableTexts = Dr. Zoidberg | 12.04.2019 | x2.0 | Weight | ERG-T-03 | Sensor Holder | 1 | 3
  Group = -> [Ortho,dim001,dim002,dim003,dim006,dim004,dim005,dim007,dim008,dim009,dim010,dim011,dim012,dim013,dim014,dim015,dim016,dim017,dim018,dim019,dim020,dim021,dim022,dim023,dim025,dim026]
  Template = <path>//share/freecad/Mod/Drawing/Templates/A4_Landscape.svg
note: 1 file-system path scrubbed to <path> (originals preserved in the JSON sidecar)
